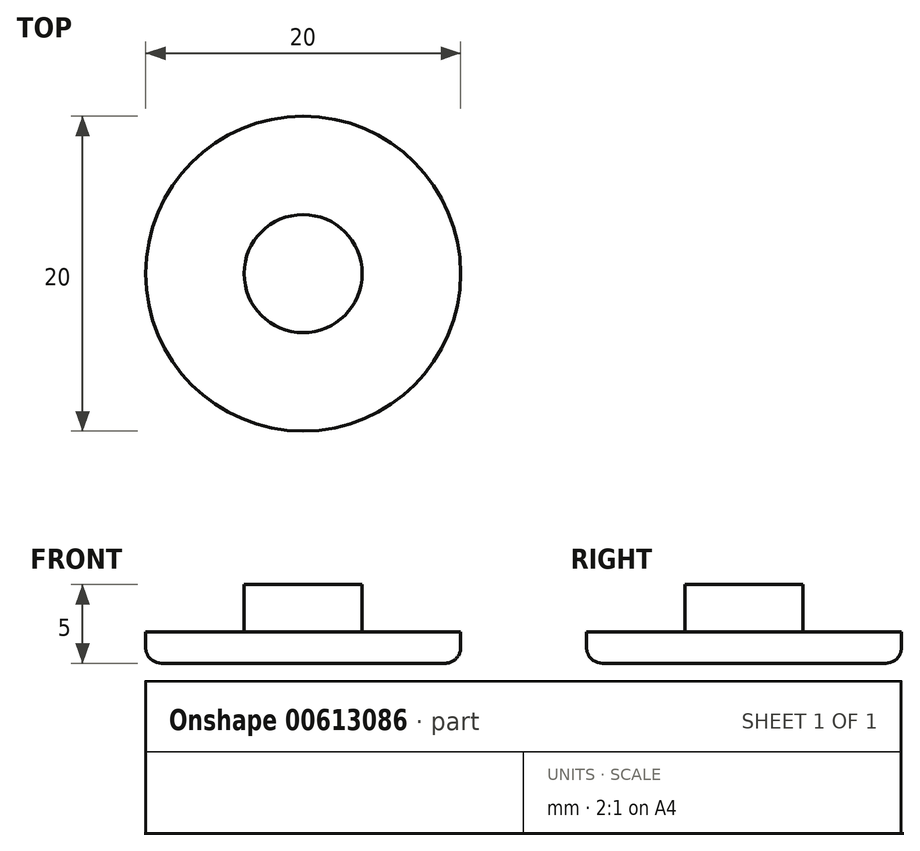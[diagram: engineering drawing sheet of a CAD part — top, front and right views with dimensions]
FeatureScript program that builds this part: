
annotation { "Feature Type Name" : "Feature", "Feature Type Description" : "" }
export const myFeature = defineFeature(function(context is Context, id is Id, definition is map)
    precondition{}
    {
        {
            var Q0;
            Q0=qCreatedBy(makeId("Top.planeOp"),FACE);
            var sketch = newSketch(context, id + "F0", { "sketchPlane" : qUnion([Q0])});
            skCircle(sketch, "E0", {"center": v(0, 0) * mm, "radius": 10 * mm});
            skSolve(sketch);
        }
        {
            var Q0;
            Q0=makeQuery(id+"F0.imprint","IMPRINT",FACE,{"disambiguationData":[TD([[makeQuery(id+"F0.imprint","IMPRINT",EDGE,{"derivedFrom":sQuery(id+"F0.wireOp",EDGE,"E0")}),1.0]])]});
            extrude(context, id + "F1", {"entities" : qUnion([Q0]), "depth" : 2 * mm, "offsetDistance" : 25 * mm});
        }
        {
            var Q0;
            Q0=makeQuery(id+"F1.opExtrude","CAP_FACE",FACE,{"disambiguationData":[OSD([sQuery(id+"F0.wireOp",EDGE,"E0")])],"isStart":false});
            var sketch = newSketch(context, id + "F2", { "sketchPlane" : qUnion([Q0])});
            skCircle(sketch, "E1", {"center": v(0, 0) * mm, "radius": 3.75 * mm});
            skSolve(sketch);
        }
        {
            var Q0;
            Q0=makeQuery(id+"F2.imprint","IMPRINT",FACE,{"disambiguationData":[TD([[makeQuery(id+"F2.imprint","IMPRINT",EDGE,{"derivedFrom":sQuery(id+"F2.wireOp",EDGE,"E1")}),1.0]])]});
            extrude(context, id + "F3", {"entities" : qUnion([Q0]), "operationType" : NewBodyOperationType.ADD, "depth" : 3 * mm, "offsetDistance" : 25 * mm});
        }
        {
            var Q0;
            Q0=makeQuery(id+"F1.opExtrude","CAP_EDGE",EDGE,{"disambiguationData":[OSD([sQuery(id+"F0.wireOp",EDGE,"E0")])],"isStart":true});
            var Q1;
            Q1=makeQuery(id+"F1.opExtrude","CAP_FACE",FACE,{"disambiguationData":[OSD([sQuery(id+"F0.wireOp",EDGE,"E0")])],"isStart":true});
            fillet(context, id + "F4", {"entities" : qUnion([Q0, Q1]), "radius" : 1 * mm, "tangentPropagation" : true, "allowEdgeOverflow" : false});
        }
    });
